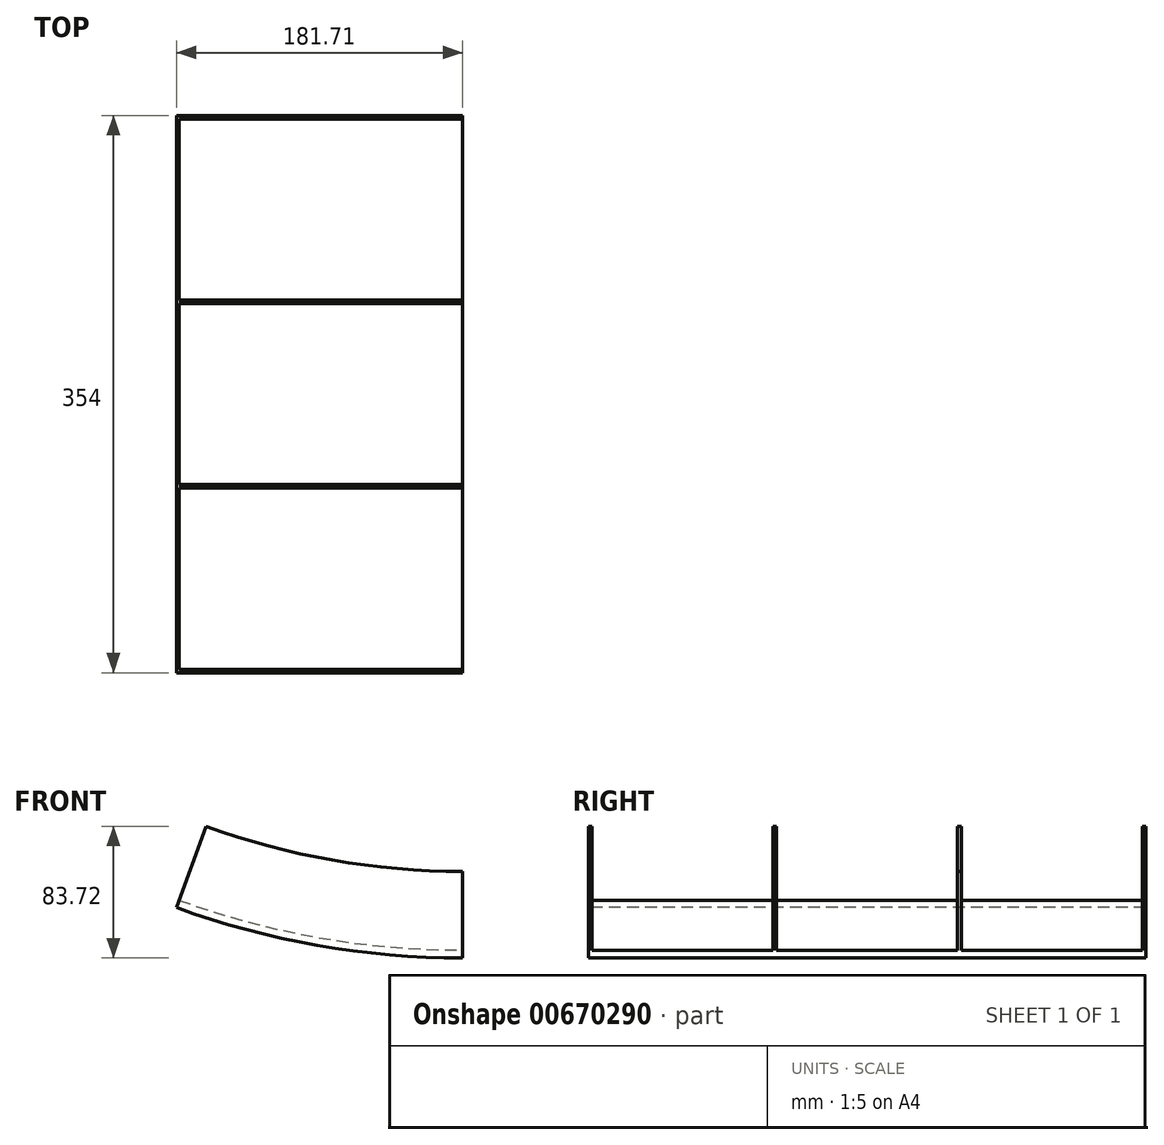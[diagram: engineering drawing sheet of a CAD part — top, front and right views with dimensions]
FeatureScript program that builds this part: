
annotation { "Feature Type Name" : "Feature", "Feature Type Description" : "" }
export const myFeature = defineFeature(function(context is Context, id is Id, definition is map)
    precondition{}
    {
        {
            var Q0;
            Q0=qCreatedBy(makeId("Front.planeOp"),FACE);
            var sketch = newSketch(context, id + "F0", { "sketchPlane" : qUnion([Q0])});
            skArc(sketch, "E0", {"start": v(-180, 31.74) * mm, "mid": v(-91.39, 8) * mm, "end": v(0, 0) * mm});
            skLineSegment(sketch, "E1", {"start": v(161.61, 0) * mm, "end": v(-336.1, 0) * mm, "construction": true});
            skLineSegment(sketch, "E2", {"start": v(-316.68, 81.49) * mm, "end": v(-92.8, 0) * mm, "construction": true});
            skSolve(sketch);
        }
        {
            var Q0;
            Q0=qCreatedBy(makeId("Front.planeOp"),FACE);
            var sketch = newSketch(context, id + "F1", { "sketchPlane" : qUnion([Q0])});
            skArc(sketch, "E3.0", {"start": v(-180, 31.74) * mm, "mid": v(-91.39, 8) * mm, "end": v(0, 0) * mm});
            skLineSegment(sketch, "E4", {"start": v(-162.9, 78.72) * mm, "end": v(-181.71, 27.04) * mm});
            skLineSegment(sketch, "E5", {"start": v(0, 50) * mm, "end": v(0, -5) * mm});
            skArc(sketch, "E6", {"start": v(-181.71, 27.04) * mm, "mid": v(-92.26, 3.07) * mm, "end": v(0, -5) * mm});
            skArc(sketch, "E7", {"start": v(-162.9, 78.72) * mm, "mid": v(-82.7, 57.24) * mm, "end": v(0, 50) * mm});
            skSolve(sketch);
        }
        {
            var Q0;
            Q0=qCreatedBy(makeId("Right.planeOp"),FACE);
            var sketch = newSketch(context, id + "F2", { "sketchPlane" : qUnion([Q0])});
            skLineSegment(sketch, "E8", {"start": v(-57.5, 0) * mm, "end": v(57.5, 0) * mm});
            skLineSegment(sketch, "E9", {"start": v(57.5, 0) * mm, "end": v(57.5, 50) * mm});
            skLineSegment(sketch, "E10", {"start": v(57.5, 50) * mm, "end": v(59.75, 50) * mm});
            skLineSegment(sketch, "E11", {"start": v(59.75, 50) * mm, "end": v(59.75, 0) * mm});
            skLineSegment(sketch, "E12", {"start": v(59.75, 0) * mm, "end": v(174.75, 0) * mm});
            skLineSegment(sketch, "E13", {"start": v(174.75, 0) * mm, "end": v(174.75, 50) * mm});
            skLineSegment(sketch, "E14", {"start": v(174.75, 50) * mm, "end": v(177, 50) * mm});
            skLineSegment(sketch, "E15", {"start": v(177, 50) * mm, "end": v(177, -5) * mm});
            skLineSegment(sketch, "E16", {"start": v(177, -5) * mm, "end": v(-177, -5) * mm});
            skLineSegment(sketch, "E17", {"start": v(-177, -5) * mm, "end": v(-177, 50) * mm});
            skLineSegment(sketch, "E18", {"start": v(-177, 50) * mm, "end": v(-174.75, 50) * mm});
            skLineSegment(sketch, "E19", {"start": v(-174.75, 50) * mm, "end": v(-174.75, 0) * mm});
            skLineSegment(sketch, "E20", {"start": v(-174.75, 0) * mm, "end": v(-59.75, 0) * mm});
            skLineSegment(sketch, "E21", {"start": v(-59.75, 0) * mm, "end": v(-59.75, 50) * mm});
            skLineSegment(sketch, "E22", {"start": v(-59.75, 50) * mm, "end": v(-57.5, 50) * mm});
            skLineSegment(sketch, "E23", {"start": v(-57.5, 50) * mm, "end": v(-57.5, 0) * mm});
            skLineSegment(sketch, "E24", {"start": v(0, -62.42) * mm, "end": v(0, 331.05) * mm, "construction": true});
            skSolve(sketch);
        }
        {
            var Q0;
            Q0=qCreatedBy(makeId("Front.planeOp"),FACE);
            var sketch = newSketch(context, id + "F3", { "sketchPlane" : qUnion([Q0])});
            skArc(sketch, "E25.0", {"start": v(-180, 31.74) * mm, "mid": v(-91.39, 8) * mm, "end": v(0, 0) * mm});
            skSolve(sketch);
        }
        {
            var Q0;
            Q0 = qSketchRegion(id + "F2", true);
            var Q1;
            Q1 = qConstructionFilter(qBodyType(qCreatedBy(id + "F3" ,EDGE), BodyType.WIRE), ConstructionObject.NO);
            sweep(context, id + "F4", {"profiles" : qUnion([Q0]), "path" : qUnion([Q1])});
        }
    });
